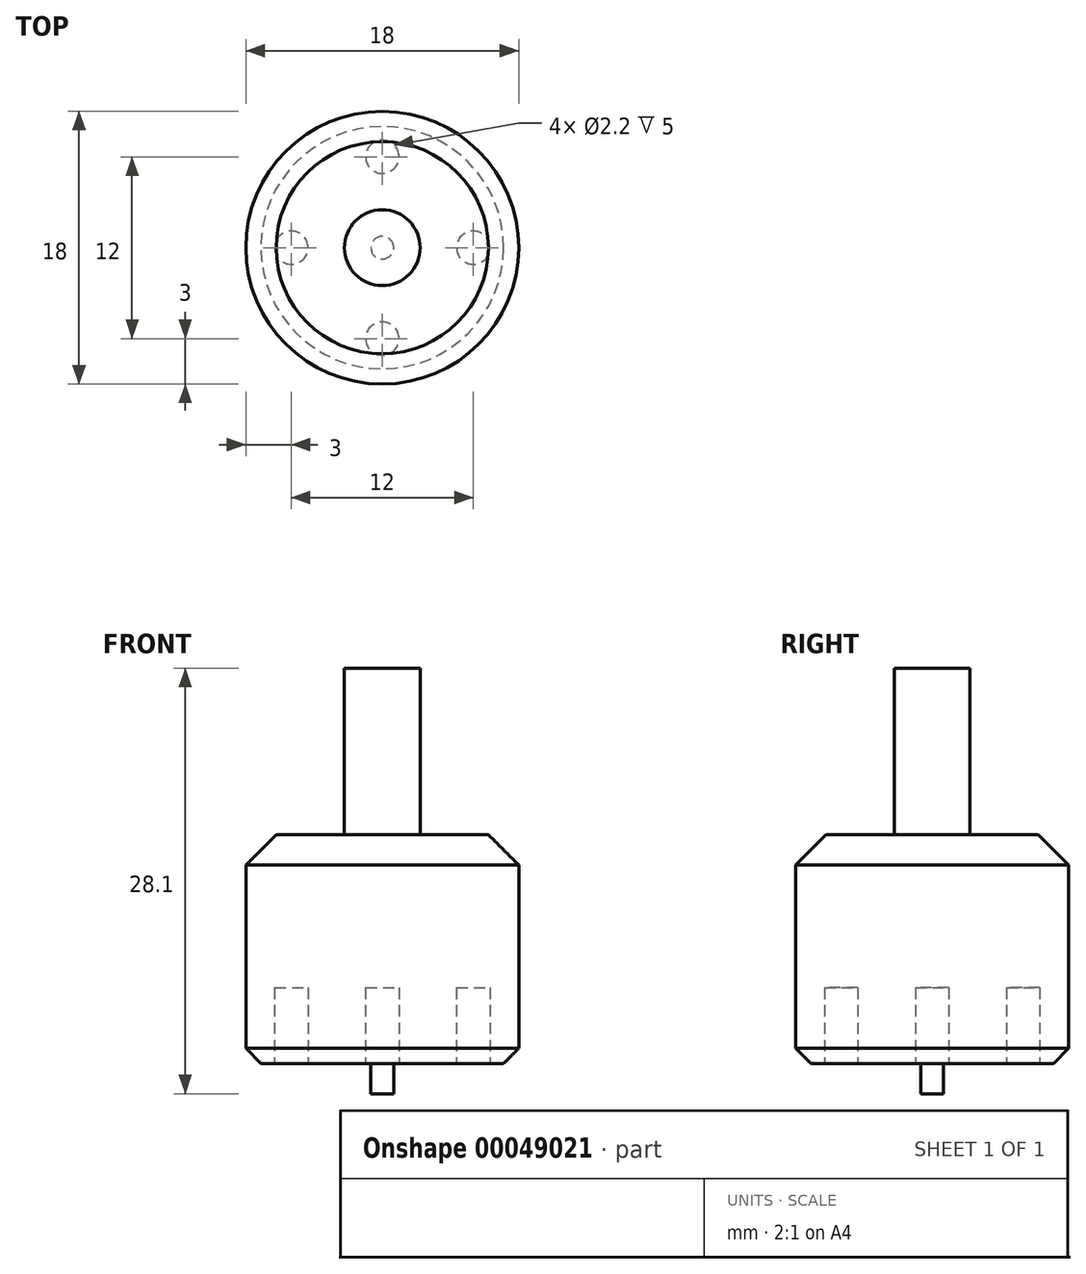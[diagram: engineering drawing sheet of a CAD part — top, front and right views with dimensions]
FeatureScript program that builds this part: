
annotation { "Feature Type Name" : "Feature", "Feature Type Description" : "" }
export const myFeature = defineFeature(function(context is Context, id is Id, definition is map)
    precondition{}
    {
        {
            var Q0;
            Q0=qCreatedBy(makeId("Top.planeOp"),FACE);
            var sketch = newSketch(context, id + "F0", { "sketchPlane" : qUnion([Q0])});
            skCircle(sketch, "E0", {"center": v(0, 0) * mm, "radius": 9 * mm});
            skSolve(sketch);
        }
        {
            var Q0;
            Q0 = qSketchRegion(id + "F0", true);
            extrude(context, id + "F1", {"entities" : qUnion([Q0]), "depth" : 15.1 * mm});
        }
        {
            var Q0;
            Q0=makeQuery(id+"F1.opExtrude","CAP_EDGE",EDGE,{"disambiguationData":[OSD([sQuery(id+"F0.wireOp",EDGE,"E0")])],"isStart":false});
            chamfer(context, id + "F2", {"entities" : qUnion([Q0]), "width" : 2 * mm, "tangentPropagation" : true});
        }
        {
            var Q0;
            Q0=makeQuery(id+"F1.opExtrude","CAP_EDGE",EDGE,{"disambiguationData":[OSD([sQuery(id+"F0.wireOp",EDGE,"E0")])],"isStart":true});
            chamfer(context, id + "F3", {"entities" : qUnion([Q0]), "width" : 1 * mm, "tangentPropagation" : true});
        }
        {
            var Q0;
            Q0=makeQuery(id+"F1.opExtrude","CAP_FACE",FACE,{"disambiguationData":[OSD([sQuery(id+"F0.wireOp",EDGE,"E0")])],"isStart":true});
            var sketch = newSketch(context, id + "F4", { "sketchPlane" : qUnion([Q0])});
            skLineSegment(sketch, "E1", {"start": v(0, 0) * mm, "end": v(0, 6) * mm, "construction": true});
            skCircle(sketch, "E2", {"center": v(0, 6) * mm, "radius": 1.1 * mm});
            skCircle(sketch, "E3.1.0", {"center": v(-6, 0) * mm, "radius": 1.1 * mm});
            skCircle(sketch, "E3.2.0", {"center": v(0, -6) * mm, "radius": 1.1 * mm});
            skCircle(sketch, "E3.3.0", {"center": v(6, 0) * mm, "radius": 1.1 * mm});
            skPoint(sketch, "E3.center", {"position": v(0, 0) * mm});
            skSolve(sketch);
        }
        {
            var Q0;
            Q0 = qSketchRegion(id + "F4", true);
            extrude(context, id + "F5", {"entities" : qUnion([Q0]), "operationType" : NewBodyOperationType.REMOVE, "oppositeDirection" : true, "depth" : 5 * mm});
        }
        {
            var Q0;
            Q0=makeQuery(id+"F1.opExtrude","CAP_FACE",FACE,{"disambiguationData":[OSD([sQuery(id+"F0.wireOp",EDGE,"E0")])],"isStart":false});
            var sketch = newSketch(context, id + "F6", { "sketchPlane" : qUnion([Q0])});
            skCircle(sketch, "E4", {"center": v(0, 0) * mm, "radius": 2.5 * mm});
            skSolve(sketch);
        }
        {
            var Q0;
            Q0 = qSketchRegion(id + "F6", true);
            extrude(context, id + "F7", {"entities" : qUnion([Q0]), "operationType" : NewBodyOperationType.ADD, "depth" : 11 * mm});
        }
        {
            var Q0;
            Q0=makeQuery(id+"F1.opExtrude","CAP_FACE",FACE,{"disambiguationData":[OSD([sQuery(id+"F0.wireOp",EDGE,"E0")])],"isStart":true});
            var sketch = newSketch(context, id + "F8", { "sketchPlane" : qUnion([Q0])});
            skCircle(sketch, "E5", {"center": v(0, 0) * mm, "radius": 0.75 * mm});
            skSolve(sketch);
        }
        {
            var Q0;
            Q0 = qSketchRegion(id + "F8", true);
            extrude(context, id + "F9", {"entities" : qUnion([Q0]), "operationType" : NewBodyOperationType.ADD, "depth" : 2 * mm});
        }
    });
